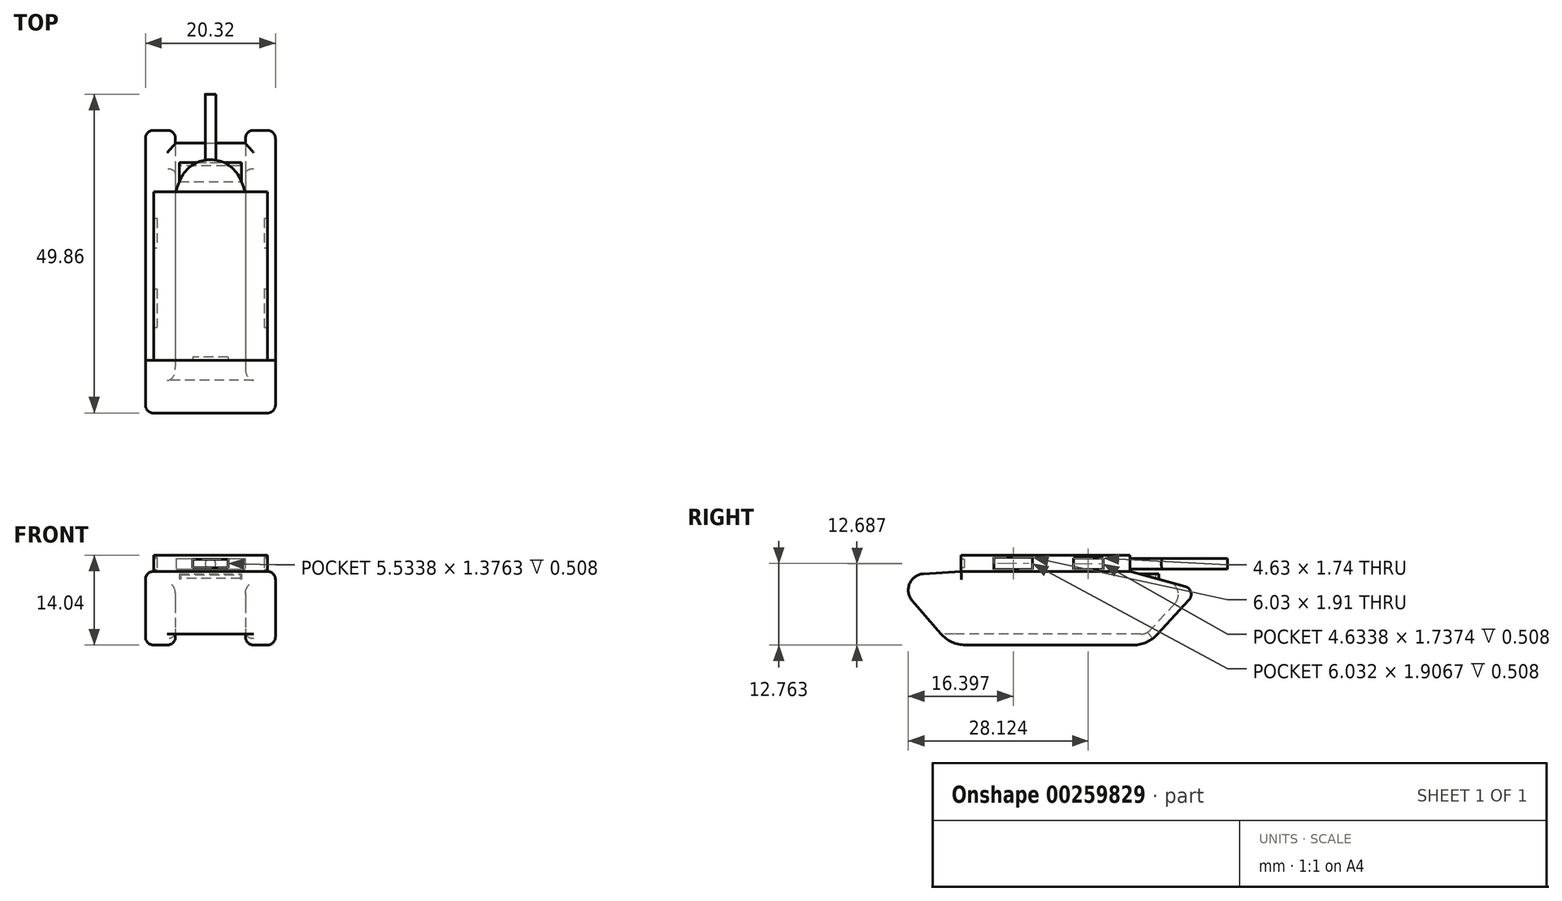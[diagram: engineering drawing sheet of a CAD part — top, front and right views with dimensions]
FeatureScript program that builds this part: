
annotation { "Feature Type Name" : "Feature", "Feature Type Description" : "" }
export const myFeature = defineFeature(function(context is Context, id is Id, definition is map)
    precondition{}
    {
        {
            var Q0;
            Q0=qCreatedBy(makeId("Right.planeOp"),FACE);
            var sketch = newSketch(context, id + "F0", { "sketchPlane" : qUnion([Q0])});
            skLineSegment(sketch, "E0", {"start": v(-16.04, 0) * mm, "end": v(14.77, 0) * mm});
            skLineSegment(sketch, "E1", {"start": v(14.77, 0) * mm, "end": v(22.64, 8.58) * mm});
            skLineSegment(sketch, "E2", {"start": v(22.64, 8.58) * mm, "end": v(12.15, 11.5) * mm});
            skLineSegment(sketch, "E3", {"start": v(12.15, 11.5) * mm, "end": v(-5.54, 11.5) * mm});
            skLineSegment(sketch, "E4", {"start": v(-5.54, 11.5) * mm, "end": v(-14.39, 11.5) * mm});
            skLineSegment(sketch, "E5", {"start": v(-14.39, 11.5) * mm, "end": v(-24.16, 14.6) * mm});
            skLineSegment(sketch, "E6", {"start": v(-24.16, 14.6) * mm, "end": v(-25.36, 10.8) * mm});
            skLineSegment(sketch, "E7", {"start": v(-14.39, 11.5) * mm, "end": v(-25.36, 10.8) * mm});
            skLineSegment(sketch, "E8", {"start": v(-25.36, 10.8) * mm, "end": v(-16.04, 0) * mm});
            skLineSegment(sketch, "E9", {"start": v(3.3, 11.5) * mm, "end": v(-3.22, 15.64) * mm});
            skLineSegment(sketch, "E10", {"start": v(-3.22, 15.64) * mm, "end": v(-10.54, 15.64) * mm});
            skLineSegment(sketch, "E11", {"start": v(-10.54, 15.64) * mm, "end": v(-10.54, 11.5) * mm});
            skSolve(sketch);
        }
        {
            var Q0;
            Q0=makeQuery(id+"F0.imprint","IMPRINT",FACE,{"disambiguationData":[TD([[makeQuery(id+"F0.imprint","IMPRINT",EDGE,{"derivedFrom":sQuery(id+"F0.wireOp",EDGE,"E0")}),1.0]])]});
            extrude(context, id + "F1", {"entities" : qUnion([Q0]), "depth" : 10.16 * mm});
        }
        {
            var Q0;
            Q0=makeQuery(id+"F1.opExtrude","CAP_FACE",FACE,{"disambiguationData":[OSD([sQuery(id+"F0.wireOp",EDGE,"E0"),sQuery(id+"F0.wireOp",EDGE,"E1"),sQuery(id+"F0.wireOp",EDGE,"E2"),sQuery(id+"F0.wireOp",EDGE,"E3"),sQuery(id+"F0.wireOp",EDGE,"E4"),sQuery(id+"F0.wireOp",EDGE,"E5"),sQuery(id+"F0.wireOp",EDGE,"E6"),sQuery(id+"F0.wireOp",EDGE,"E8")])],"isStart":true});
            extrude(context, id + "F2", {"entities" : qUnion([Q0]), "operationType" : NewBodyOperationType.ADD, "depth" : 10.16 * mm});
        }
        {
            var Q0;
            Q0=qCreatedBy(makeId("Front.planeOp"),FACE);
            var sketch = newSketch(context, id + "F3", { "sketchPlane" : qUnion([Q0])});
            skLineSegment(sketch, "E12.bottom", {"start": v(-5.47, 1.7) * mm, "end": v(5.47, 1.7) * mm});
            skLineSegment(sketch, "E12.top", {"start": v(-5.47, -1.7) * mm, "end": v(5.47, -1.7) * mm});
            skLineSegment(sketch, "E12.left", {"start": v(-5.47, 1.7) * mm, "end": v(-5.47, -1.7) * mm});
            skLineSegment(sketch, "E12.right", {"start": v(5.47, 1.7) * mm, "end": v(5.47, -1.7) * mm});
            skPoint(sketch, "E12.middle", {"position": v(0, 0) * mm});
            skSolve(sketch);
        }
        {
            var Q0;
            Q0=makeQuery(id+"F3.imprint","IMPRINT",FACE,{"disambiguationData":[TD([[makeQuery(id+"F3.imprint","IMPRINT",EDGE,{"derivedFrom":sQuery(id+"F3.wireOp",EDGE,"E12.bottom")}),-1.0]])]});
            extrude(context, id + "F4", {"entities" : qUnion([Q0]), "operationType" : NewBodyOperationType.REMOVE, "oppositeDirection" : true, "depth" : 25.4 * mm});
        }
        {
            var Q0;
            Q0=makeQuery(id+"F4.boolean.opBoolean","COPY",FACE,{"derivedFrom":makeQuery(id+"F4.opExtrude","CAP_FACE",FACE,{"disambiguationData":[OSD([sQuery(id+"F3.wireOp",EDGE,"E12.bottom"),sQuery(id+"F3.wireOp",EDGE,"E12.top"),sQuery(id+"F3.wireOp",EDGE,"E12.left"),sQuery(id+"F3.wireOp",EDGE,"E12.right")])],"isStart":true})});
            extrude(context, id + "F5", {"entities" : qUnion([Q0]), "operationType" : NewBodyOperationType.REMOVE, "oppositeDirection" : true, "depth" : 25.4 * mm});
        }
        {
            var Q0;
            {var subQ0=sQuery(id+"F0.wireOp",EDGE,"E0");var subQ1=sQuery(id+"F0.wireOp",EDGE,"E1");Q0=makeQuery(id+"F4.boolean.opBoolean","SPLIT",EDGE,{"disambiguationData":[TD([makeQuery(id+"F4.opExtrude","SWEPT_FACE",FACE,{"disambiguationData":[OSD([sQuery(id+"F3.wireOp",EDGE,"E12.right")])]})])],"derivedFrom":makeQuery(id+"F2.boolean.opBoolean","MERGE",EDGE,{"derivedFrom":[makeQuery(id+"F1.opExtrude","SWEPT_EDGE",EDGE,{"disambiguationData":[OSD([subQ0,subQ1])]}),makeQuery(id+"F2.opExtrude","SWEPT_EDGE",EDGE,{"disambiguationData":[OSD([subQ0,subQ1])]})]})});}
            var Q1;
            {var subQ0=sQuery(id+"F0.wireOp",EDGE,"E0");var subQ1=sQuery(id+"F0.wireOp",EDGE,"E8");var subQ2=sQuery(id+"F3.wireOp",EDGE,"E12.right");Q1=makeQuery(id+"F5.boolean.opBoolean","SPLIT",EDGE,{"disambiguationData":[TD([makeQuery(id+"F4.boolean.opBoolean","COPY",FACE,{"derivedFrom":makeQuery(id+"F4.opExtrude","SWEPT_FACE",FACE,{"disambiguationData":[OSD([subQ2])]})})])],"derivedFrom":makeQuery(id+"F2.boolean.opBoolean","MERGE",EDGE,{"derivedFrom":[makeQuery(id+"F1.opExtrude","SWEPT_EDGE",EDGE,{"disambiguationData":[OSD([subQ0,subQ1])]}),makeQuery(id+"F2.opExtrude","SWEPT_EDGE",EDGE,{"disambiguationData":[OSD([subQ0,subQ1])]})]})});}
            var Q2;
            {var subQ0=sQuery(id+"F0.wireOp",EDGE,"E1");var subQ1=sQuery(id+"F0.wireOp",EDGE,"E0");Q2=makeQuery(id+"F4.boolean.opBoolean","SPLIT",EDGE,{"disambiguationData":[TD([makeQuery(id+"F4.opExtrude","SWEPT_FACE",FACE,{"disambiguationData":[OSD([sQuery(id+"F3.wireOp",EDGE,"E12.left")])]})])],"derivedFrom":makeQuery(id+"F2.boolean.opBoolean","MERGE",EDGE,{"derivedFrom":[makeQuery(id+"F1.opExtrude","SWEPT_EDGE",EDGE,{"disambiguationData":[OSD([subQ1,subQ0])]}),makeQuery(id+"F2.opExtrude","SWEPT_EDGE",EDGE,{"disambiguationData":[OSD([subQ1,subQ0])]})]})});}
            fillet(context, id + "F6", {"entities" : qUnion([Q0, Q1, Q2]), "radius" : 5.08 * mm, "tangentPropagation" : true, "allowEdgeOverflow" : false});
        }
        {
            var Q0;
            {var subQ0=sQuery(id+"F0.wireOp",EDGE,"E2");var subQ1=sQuery(id+"F0.wireOp",EDGE,"E1");Q0=makeQuery(id+"F2.boolean.opBoolean","MERGE",EDGE,{"derivedFrom":[makeQuery(id+"F1.opExtrude","SWEPT_EDGE",EDGE,{"disambiguationData":[OSD([subQ1,subQ0])]}),makeQuery(id+"F2.opExtrude","SWEPT_EDGE",EDGE,{"disambiguationData":[OSD([subQ1,subQ0])]})]});}
            var Q1;
            {var subQ0=sQuery(id+"F0.wireOp",EDGE,"E3");var subQ1=sQuery(id+"F0.wireOp",EDGE,"E2");Q1=makeQuery(id+"F2.boolean.opBoolean","MERGE",EDGE,{"derivedFrom":[makeQuery(id+"F1.opExtrude","SWEPT_EDGE",EDGE,{"disambiguationData":[OSD([subQ1,subQ0])]}),makeQuery(id+"F2.opExtrude","SWEPT_EDGE",EDGE,{"disambiguationData":[OSD([subQ1,subQ0])]})]});}
            fillet(context, id + "F7", {"entities" : qUnion([Q0, Q1]), "radius" : 1.27 * mm, "tangentPropagation" : true, "allowEdgeOverflow" : false});
        }
        {
            var Q0;
            Q0=makeQuery(id+"F2.opExtrude","CAP_EDGE",EDGE,{"disambiguationData":[OSD([sQuery(id+"F0.wireOp",EDGE,"E3"),sQuery(id+"F0.wireOp",EDGE,"E4")])],"isStart":false});
            var Q1;
            Q1=makeQuery(id+"F1.opExtrude","CAP_EDGE",EDGE,{"disambiguationData":[OSD([sQuery(id+"F0.wireOp",EDGE,"E3"),sQuery(id+"F0.wireOp",EDGE,"E4")])],"isStart":false});
            fillet(context, id + "F8", {"entities" : qUnion([Q0, Q1]), "radius" : 1.27 * mm, "tangentPropagation" : true, "allowEdgeOverflow" : false});
        }
        {
            var Q0;
            {var subQ0=sQuery(id+"F0.wireOp",EDGE,"E1");Q0=makeQuery(id+"F2.boolean.opBoolean","MERGE",FACE,{"derivedFrom":[makeQuery(id+"F1.opExtrude","SWEPT_FACE",FACE,{"disambiguationData":[OSD([subQ0])]}),makeQuery(id+"F2.opExtrude","SWEPT_FACE",FACE,{"disambiguationData":[OSD([subQ0])]})]});}
            var sketch = newSketch(context, id + "F9", { "sketchPlane" : qUnion([Q0])});
            skLineSegment(sketch, "E13.bottom", {"start": v(5.47, 22) * mm, "end": v(-5.47, 22) * mm});
            skLineSegment(sketch, "E13.top", {"start": v(5.47, 2.57) * mm, "end": v(-5.47, 2.57) * mm});
            skLineSegment(sketch, "E13.left", {"start": v(5.47, 22) * mm, "end": v(5.47, 2.57) * mm});
            skLineSegment(sketch, "E13.right", {"start": v(-5.47, 22) * mm, "end": v(-5.47, 2.57) * mm});
            skPoint(sketch, "E13.middle", {"position": v(0, 12.29) * mm});
            skSolve(sketch);
        }
        {
            var Q0;
            {var subQ1=sQuery(id+"F0.wireOp",EDGE,"E1");var subQ2=makeQuery(id+"F2.boolean.opBoolean","MERGE",FACE,{"derivedFrom":[makeQuery(id+"F1.opExtrude","SWEPT_FACE",FACE,{"disambiguationData":[OSD([subQ1])]}),makeQuery(id+"F2.opExtrude","SWEPT_FACE",FACE,{"disambiguationData":[OSD([subQ1])]})]});var subQ3=makeQuery(id+"F4.boolean.opBoolean","INTERSECT",EDGE,{"derivedFrom":[subQ2,makeQuery(id+"F4.opExtrude","SWEPT_FACE",FACE,{"disambiguationData":[OSD([sQuery(id+"F3.wireOp",EDGE,"E12.bottom")])]})]});Q0=makeQuery(id+"F9.imprint","IMPRINT",FACE,{"disambiguationData":[TD([[makeQuery(id+"F9.imprint","IMPRINT",EDGE,{"derivedFrom":subQ3}),-1.0]])]});}
            var Q1;
            {var subQ0=sQuery(id+"F9.wireOp",EDGE,"E13.bottom");Q1=makeQuery(id+"F9.imprint","IMPRINT",FACE,{"disambiguationData":[TD([[makeQuery(id+"F9.imprint","IMPRINT",EDGE,{"derivedFrom":subQ0}),1.0]])]});}
            extrude(context, id + "F10", {"entities" : qUnion([Q0, Q1]), "operationType" : NewBodyOperationType.REMOVE, "oppositeDirection" : true, "depth" : 1.27 * mm});
        }
        {
            var Q0;
            Q0=makeQuery(id+"F10.boolean.opBoolean","COPY",FACE,{"derivedFrom":makeQuery(id+"F10.opExtrude","SWEPT_FACE",FACE,{"disambiguationData":[OSD([sQuery(id+"F0.wireOp",EDGE,"E1"),sQuery(id+"F3.wireOp",EDGE,"E12.bottom")])]})});
            extrude(context, id + "F11", {"entities" : qUnion([Q0]), "operationType" : NewBodyOperationType.REMOVE, "oppositeDirection" : true, "depth" : 1.27 * mm});
        }
        {
            var Q0;
            {var subQ0=sQuery(id+"F0.wireOp",EDGE,"E8");Q0=makeQuery(id+"F2.boolean.opBoolean","MERGE",FACE,{"derivedFrom":[makeQuery(id+"F1.opExtrude","SWEPT_FACE",FACE,{"disambiguationData":[OSD([subQ0])]}),makeQuery(id+"F2.opExtrude","SWEPT_FACE",FACE,{"disambiguationData":[OSD([subQ0])]})]});}
            var sketch = newSketch(context, id + "F12", { "sketchPlane" : qUnion([Q0])});
            skLineSegment(sketch, "E14.bottom", {"start": v(5.47, 31.97) * mm, "end": v(-5.47, 31.97) * mm});
            skLineSegment(sketch, "E14.top", {"start": v(5.47, -6.36) * mm, "end": v(-5.47, -6.36) * mm});
            skLineSegment(sketch, "E14.left", {"start": v(5.47, 31.97) * mm, "end": v(5.47, -6.36) * mm});
            skLineSegment(sketch, "E14.right", {"start": v(-5.47, 31.97) * mm, "end": v(-5.47, -6.36) * mm});
            skPoint(sketch, "E14.middle", {"position": v(0, 12.8) * mm});
            skSolve(sketch);
        }
        {
            var Q0;
            {var subQ0=sQuery(id+"F12.wireOp",EDGE,"E14.left");var subQ1=sQuery(id+"F0.wireOp",EDGE,"E8");var subQ2=makeQuery(id+"F2.opExtrude","SWEPT_FACE",FACE,{"disambiguationData":[OSD([subQ1])]});var subQ3=makeQuery(id+"F1.opExtrude","SWEPT_FACE",FACE,{"disambiguationData":[OSD([subQ1])]});var subQ4=makeQuery(id+"F2.boolean.opBoolean","MERGE",FACE,{"derivedFrom":[subQ3,subQ2]});var subQ5=sQuery(id+"F0.wireOp",EDGE,"E7");var subQ6=sQuery(id+"F0.wireOp",EDGE,"E6");var subQ7=makeQuery(id+"FmgriYv2DjoOcs5_1.opFillet","BLEND_EDGE",EDGE,{"blendedFrom":[makeQuery(id+"F2.boolean.opBoolean","MERGE",EDGE,{"derivedFrom":[makeQuery(id+"F1.opExtrude","SWEPT_EDGE",EDGE,{"disambiguationData":[OSD([subQ6,subQ5,subQ1])]}),makeQuery(id+"F2.opExtrude","SWEPT_EDGE",EDGE,{"disambiguationData":[OSD([subQ6,subQ5,subQ1])]})]}),subQ4],"blendedInto":[subQ4]});var subQ8=makeQuery(id+"F12.imprint","INTERSECT",VERTEX,{"derivedFrom":[subQ7,subQ0]});Q0=makeQuery(id+"F12.imprint","IMPRINT",FACE,{"disambiguationData":[TD([[makeQuery(id+"F12.imprint","IMPRINT",EDGE,{"disambiguationData":[TD([[subQ8,-1.0]])],"derivedFrom":subQ7}),1.0]])]});}
            var Q1;
            {var subQ0=sQuery(id+"F12.wireOp",EDGE,"E14.bottom");Q1=makeQuery(id+"F12.imprint","IMPRINT",FACE,{"disambiguationData":[TD([[makeQuery(id+"F12.imprint","IMPRINT",EDGE,{"derivedFrom":subQ0}),1.0]])]});}
            extrude(context, id + "F13", {"entities" : qUnion([Q0, Q1]), "operationType" : NewBodyOperationType.REMOVE, "oppositeDirection" : true, "depth" : 1.27 * mm});
        }
        {
            var Q0;
            {var subQ0=sQuery(id+"F0.wireOp",EDGE,"E1");Q0=makeQuery(id+"F10.boolean.opBoolean","INTERSECT",EDGE,{"derivedFrom":[makeQuery(id+"F7.opFillet","BLEND_FACE",FACE,{"disambiguationData":[OSD([subQ0,sQuery(id+"F0.wireOp",EDGE,"E2")])]}),makeQuery(id+"F10.opExtrude","CAP_FACE",FACE,{"disambiguationData":[OSD([subQ0,sQuery(id+"F3.wireOp",EDGE,"E12.bottom"),sQuery(id+"F9.wireOp",EDGE,"E13.bottom"),sQuery(id+"F9.wireOp",EDGE,"E13.left"),sQuery(id+"F9.wireOp",EDGE,"E13.right")])],"isStart":false})]});}
            var Q1;
            {var subQ0=sQuery(id+"F0.wireOp",EDGE,"E6");Q1=makeQuery(id+"F13.boolean.opBoolean","INTERSECT",EDGE,{"derivedFrom":[makeQuery(id+"F2.boolean.opBoolean","MERGE",FACE,{"derivedFrom":[makeQuery(id+"F1.opExtrude","SWEPT_FACE",FACE,{"disambiguationData":[OSD([subQ0])]}),makeQuery(id+"F2.opExtrude","SWEPT_FACE",FACE,{"disambiguationData":[OSD([subQ0])]})]}),makeQuery(id+"F13.opExtrude","CAP_FACE",FACE,{"disambiguationData":[OSD([sQuery(id+"F0.wireOp",EDGE,"E0"),sQuery(id+"F0.wireOp",EDGE,"E8"),sQuery(id+"F12.wireOp",EDGE,"E14.bottom"),sQuery(id+"F12.wireOp",EDGE,"E14.left"),sQuery(id+"F12.wireOp",EDGE,"E14.right")])],"isStart":false})]});}
            var Q2;
            {var subQ0=sQuery(id+"F0.wireOp",EDGE,"E8");var subQ1=sQuery(id+"F0.wireOp",EDGE,"E0");var subQ2=sQuery(id+"F3.wireOp",EDGE,"E12.bottom");Q2=makeQuery(id+"Fq2m1Uq80MRG6K2_1.boolean.opBoolean","INTERSECT",EDGE,{"derivedFrom":[makeQuery(id+"F5.boolean.opBoolean","MERGE",FACE,{"derivedFrom":[makeQuery(id+"F4.boolean.opBoolean","COPY",FACE,{"derivedFrom":makeQuery(id+"F4.opExtrude","SWEPT_FACE",FACE,{"disambiguationData":[OSD([subQ2])]})}),makeQuery(id+"F5.opExtrude","SWEPT_FACE",FACE,{"disambiguationData":[OSD([subQ2])]})]}),makeQuery(id+"Fq2m1Uq80MRG6K2_1.opExtrude","SWEPT_FACE",FACE,{"disambiguationData":[OSD([subQ1,subQ0]),TDD([makeQuery(id+"F13.boolean.opBoolean","COPY",EDGE,{"derivedFrom":makeQuery(id+"F13.opExtrude","CAP_EDGE",EDGE,{"disambiguationData":[OSD([subQ1,subQ0])],"isStart":false})})])]})]});}
            var Q3;
            {var subQ0=sQuery(id+"F3.wireOp",EDGE,"E12.bottom");var subQ1=sQuery(id+"F0.wireOp",EDGE,"E1");Q3=makeQuery(id+"F11.boolean.opBoolean","INTERSECT",EDGE,{"derivedFrom":[makeQuery(id+"F5.boolean.opBoolean","MERGE",FACE,{"derivedFrom":[makeQuery(id+"F4.boolean.opBoolean","COPY",FACE,{"derivedFrom":makeQuery(id+"F4.opExtrude","SWEPT_FACE",FACE,{"disambiguationData":[OSD([subQ0])]})}),makeQuery(id+"F5.opExtrude","SWEPT_FACE",FACE,{"disambiguationData":[OSD([subQ0])]})]}),makeQuery(id+"F11.opExtrude","SWEPT_FACE",FACE,{"disambiguationData":[OSD([subQ1,subQ0]),TDD([makeQuery(id+"F10.boolean.opBoolean","COPY",EDGE,{"derivedFrom":makeQuery(id+"F10.opExtrude","CAP_EDGE",EDGE,{"disambiguationData":[OSD([subQ1,subQ0])],"isStart":false})})])]})]});}
            fillet(context, id + "F14", {"entities" : qUnion([Q0, Q1, Q2, Q3]), "radius" : 2.03 * mm, "tangentPropagation" : true, "allowEdgeOverflow" : false});
        }
        {
            var Q0;
            {var subQ0=sQuery(id+"F0.wireOp",EDGE,"E1");Q0=makeQuery(id+"F11.boolean.opBoolean","MERGE",EDGE,{"derivedFrom":[makeQuery(id+"F4.boolean.opBoolean","INTERSECT",EDGE,{"derivedFrom":[makeQuery(id+"F2.boolean.opBoolean","MERGE",FACE,{"derivedFrom":[makeQuery(id+"F1.opExtrude","SWEPT_FACE",FACE,{"disambiguationData":[OSD([subQ0])]}),makeQuery(id+"F2.opExtrude","SWEPT_FACE",FACE,{"disambiguationData":[OSD([subQ0])]})]}),makeQuery(id+"F4.opExtrude","SWEPT_FACE",FACE,{"disambiguationData":[OSD([sQuery(id+"F3.wireOp",EDGE,"E12.left")])]})]}),makeQuery(id+"F10.boolean.opBoolean","COPY",EDGE,{"derivedFrom":makeQuery(id+"F10.opExtrude","CAP_EDGE",EDGE,{"disambiguationData":[OSD([sQuery(id+"F9.wireOp",EDGE,"E13.left")])],"isStart":true})})]});}
            var Q1;
            {var subQ0=sQuery(id+"F0.wireOp",EDGE,"E1");Q1=makeQuery(id+"F11.boolean.opBoolean","MERGE",EDGE,{"derivedFrom":[makeQuery(id+"F4.boolean.opBoolean","INTERSECT",EDGE,{"derivedFrom":[makeQuery(id+"F2.boolean.opBoolean","MERGE",FACE,{"derivedFrom":[makeQuery(id+"F1.opExtrude","SWEPT_FACE",FACE,{"disambiguationData":[OSD([subQ0])]}),makeQuery(id+"F2.opExtrude","SWEPT_FACE",FACE,{"disambiguationData":[OSD([subQ0])]})]}),makeQuery(id+"F4.opExtrude","SWEPT_FACE",FACE,{"disambiguationData":[OSD([sQuery(id+"F3.wireOp",EDGE,"E12.right")])]})]}),makeQuery(id+"F10.boolean.opBoolean","COPY",EDGE,{"derivedFrom":makeQuery(id+"F10.opExtrude","CAP_EDGE",EDGE,{"disambiguationData":[OSD([sQuery(id+"F9.wireOp",EDGE,"E13.right")])],"isStart":true})})]});}
            fillet(context, id + "F15", {"entities" : qUnion([Q0, Q1]), "radius" : 1.27 * mm, "tangentPropagation" : true, "allowEdgeOverflow" : false});
        }
        {
            var Q0;
            {var subQ0=sQuery(id+"F0.wireOp",EDGE,"E8");var subQ1=sQuery(id+"F0.wireOp",EDGE,"E7");var subQ2=sQuery(id+"F0.wireOp",EDGE,"E6");Q0=makeQuery(id+"F2.boolean.opBoolean","MERGE",EDGE,{"derivedFrom":[makeQuery(id+"F1.opExtrude","SWEPT_EDGE",EDGE,{"disambiguationData":[OSD([subQ2,subQ1,subQ0])]}),makeQuery(id+"F2.opExtrude","SWEPT_EDGE",EDGE,{"disambiguationData":[OSD([subQ2,subQ1,subQ0])]})]});}
            fillet(context, id + "F16", {"entities" : qUnion([Q0]), "radius" : 2.54 * mm, "tangentPropagation" : true, "allowEdgeOverflow" : false});
        }
        {
            var Q0;
            Q0=qCreatedBy(makeId("Front.planeOp"),FACE);
            var sketch = newSketch(context, id + "F17", { "sketchPlane" : qUnion([Q0])});
            skLineSegment(sketch, "E15.bottom", {"start": v(-4.86, 11.12) * mm, "end": v(4.86, 11.12) * mm});
            skLineSegment(sketch, "E15.top", {"start": v(-4.86, 10.04) * mm, "end": v(4.86, 10.04) * mm});
            skLineSegment(sketch, "E15.left", {"start": v(-4.86, 11.12) * mm, "end": v(-4.86, 10.04) * mm});
            skLineSegment(sketch, "E15.right", {"start": v(4.86, 11.12) * mm, "end": v(4.86, 10.04) * mm});
            skPoint(sketch, "E15.middle", {"position": v(0, 10.58) * mm});
            skLineSegment(sketch, "E16.bottom", {"start": v(-4.7, 10.97) * mm, "end": v(4.7, 10.97) * mm});
            skLineSegment(sketch, "E16.top", {"start": v(-4.7, 10.18) * mm, "end": v(4.7, 10.18) * mm});
            skLineSegment(sketch, "E16.left", {"start": v(-4.7, 10.97) * mm, "end": v(-4.7, 10.18) * mm});
            skLineSegment(sketch, "E16.right", {"start": v(4.7, 10.97) * mm, "end": v(4.7, 10.18) * mm});
            skLineSegment(sketch, "E17.bottom", {"start": v(-4.86, 9.41) * mm, "end": v(4.86, 9.41) * mm});
            skLineSegment(sketch, "E17.top", {"start": v(-4.86, 7.44) * mm, "end": v(4.86, 7.44) * mm});
            skLineSegment(sketch, "E17.left", {"start": v(-4.86, 9.41) * mm, "end": v(-4.86, 7.44) * mm});
            skLineSegment(sketch, "E17.right", {"start": v(4.86, 9.41) * mm, "end": v(4.86, 7.44) * mm});
            skPoint(sketch, "E17.middle", {"position": v(0, 8.43) * mm});
            skSolve(sketch);
        }
        {
            var Q0;
            Q0=makeQuery(id+"F17.imprint","IMPRINT",FACE,{"disambiguationData":[TD([[makeQuery(id+"F17.imprint","IMPRINT",EDGE,{"derivedFrom":sQuery(id+"F17.wireOp",EDGE,"E15.bottom")}),-1.0]])]});
            extrude(context, id + "F18", {"entities" : qUnion([Q0]), "oppositeDirection" : true, "depth" : 16.5 * mm});
        }
        {
            var Q0;
            {var subQ0=sQuery(id+"F0.wireOp",EDGE,"E4");var subQ1=sQuery(id+"F0.wireOp",EDGE,"E3");Q0=makeQuery(id+"F2.boolean.opBoolean","MERGE",FACE,{"derivedFrom":[makeQuery(id+"F1.opExtrude","SWEPT_FACE",FACE,{"disambiguationData":[OSD([subQ1,subQ0])]}),makeQuery(id+"F2.opExtrude","SWEPT_FACE",FACE,{"disambiguationData":[OSD([subQ1,subQ0])]})]});}
            extrude(context, id + "F19", {"entities" : qUnion([Q0]), "operationType" : NewBodyOperationType.ADD, "depth" : 2.54 * mm});
        }
        {
            var Q0;
            {var subQ0=sQuery(id+"F0.wireOp",EDGE,"E4");var subQ1=sQuery(id+"F0.wireOp",EDGE,"E3");Q0=makeQuery(id+"F19.opExtrude","SWEPT_FACE",FACE,{"disambiguationData":[OSD([subQ1,subQ0]),TDD([makeQuery(id+"F8.opFillet","BLEND_EDGE",EDGE,{"blendedFrom":[makeQuery(id+"F1.opExtrude","CAP_EDGE",EDGE,{"disambiguationData":[OSD([subQ1,subQ0])],"isStart":false}),makeQuery(id+"F2.boolean.opBoolean","MERGE",FACE,{"derivedFrom":[makeQuery(id+"F1.opExtrude","SWEPT_FACE",FACE,{"disambiguationData":[OSD([subQ1,subQ0])]}),makeQuery(id+"F2.opExtrude","SWEPT_FACE",FACE,{"disambiguationData":[OSD([subQ1,subQ0])]})]})],"blendedInto":[makeQuery(id+"F2.boolean.opBoolean","MERGE",FACE,{"derivedFrom":[makeQuery(id+"F1.opExtrude","SWEPT_FACE",FACE,{"disambiguationData":[OSD([subQ1,subQ0])]}),makeQuery(id+"F2.opExtrude","SWEPT_FACE",FACE,{"disambiguationData":[OSD([subQ1,subQ0])]})]})]})])]});}
            var sketch = newSketch(context, id + "F20", { "sketchPlane" : qUnion([Q0])});
            skLineSegment(sketch, "E18.bottom", {"start": v(7.8, 13.56) * mm, "end": v(3.17, 13.56) * mm});
            skLineSegment(sketch, "E18.top", {"start": v(7.8, 11.82) * mm, "end": v(3.17, 11.82) * mm});
            skLineSegment(sketch, "E18.left", {"start": v(7.8, 13.56) * mm, "end": v(7.8, 11.82) * mm});
            skLineSegment(sketch, "E18.right", {"start": v(3.17, 13.56) * mm, "end": v(3.17, 11.82) * mm});
            skPoint(sketch, "E18.middle", {"position": v(5.48, 12.69) * mm});
            skLineSegment(sketch, "E19.bottom", {"start": v(-3.23, 13.72) * mm, "end": v(-9.26, 13.72) * mm});
            skLineSegment(sketch, "E19.top", {"start": v(-3.23, 11.81) * mm, "end": v(-9.26, 11.81) * mm});
            skLineSegment(sketch, "E19.left", {"start": v(-3.23, 13.72) * mm, "end": v(-3.23, 11.81) * mm});
            skLineSegment(sketch, "E19.right", {"start": v(-9.26, 13.72) * mm, "end": v(-9.26, 11.81) * mm});
            skPoint(sketch, "E19.middle", {"position": v(-6.24, 12.76) * mm});
            skSolve(sketch);
        }
        {
            var Q0;
            Q0=makeQuery(id+"F20.imprint","IMPRINT",FACE,{"disambiguationData":[TD([[makeQuery(id+"F20.imprint","IMPRINT",EDGE,{"derivedFrom":sQuery(id+"F20.wireOp",EDGE,"E19.bottom")}),1.0]])]});
            var Q1;
            Q1=makeQuery(id+"F20.imprint","IMPRINT",FACE,{"disambiguationData":[TD([[makeQuery(id+"F20.imprint","IMPRINT",EDGE,{"derivedFrom":sQuery(id+"F20.wireOp",EDGE,"E18.bottom")}),1.0]])]});
            extrude(context, id + "F21", {"entities" : qUnion([Q0, Q1]), "operationType" : NewBodyOperationType.REMOVE, "oppositeDirection" : true, "depth" : 25.4 * mm});
        }
        {
            var Q0;
            Q0=makeQuery(id+"F20.imprint","IMPRINT",FACE,{"disambiguationData":[TD([[makeQuery(id+"F20.imprint","IMPRINT",EDGE,{"derivedFrom":sQuery(id+"F20.wireOp",EDGE,"E18.bottom")}),1.0]])]});
            var Q1;
            Q1=makeQuery(id+"F20.imprint","IMPRINT",FACE,{"disambiguationData":[TD([[makeQuery(id+"F20.imprint","IMPRINT",EDGE,{"derivedFrom":sQuery(id+"F20.wireOp",EDGE,"E19.bottom")}),1.0]])]});
            extrude(context, id + "F22", {"entities" : qUnion([Q0, Q1]), "operationType" : NewBodyOperationType.ADD, "oppositeDirection" : true, "depth" : 17.27 * mm});
        }
        {
            var Q0;
            Q0=makeQuery(id+"F20.imprint","IMPRINT",FACE,{"disambiguationData":[TD([[makeQuery(id+"F20.imprint","IMPRINT",EDGE,{"derivedFrom":sQuery(id+"F20.wireOp",EDGE,"E19.bottom")}),1.0]])]});
            var Q1;
            Q1=makeQuery(id+"F20.imprint","IMPRINT",FACE,{"disambiguationData":[TD([[makeQuery(id+"F20.imprint","IMPRINT",EDGE,{"derivedFrom":sQuery(id+"F20.wireOp",EDGE,"E18.bottom")}),1.0]])]});
            extrude(context, id + "F23", {"entities" : qUnion([Q0, Q1]), "operationType" : NewBodyOperationType.REMOVE, "oppositeDirection" : true, "depth" : 0.5 * mm});
        }
        {
            var Q0;
            Q0=makeQuery(id+"F17.imprint","IMPRINT",FACE,{"disambiguationData":[TD([[makeQuery(id+"F17.imprint","IMPRINT",EDGE,{"derivedFrom":sQuery(id+"F17.wireOp",EDGE,"E16.bottom")}),-1.0]])]});
            extrude(context, id + "F24", {"entities" : qUnion([Q0]), "operationType" : NewBodyOperationType.ADD, "oppositeDirection" : true, "depth" : 16 * mm});
        }
        {
            var Q0;
            Q0=makeQuery(id+"F19.opExtrude","SWEPT_FACE",FACE,{"disambiguationData":[OSD([sQuery(id+"F0.wireOp",EDGE,"E2"),sQuery(id+"F0.wireOp",EDGE,"E3"),sQuery(id+"F0.wireOp",EDGE,"E4")])]});
            var sketch = newSketch(context, id + "F25", { "sketchPlane" : qUnion([Q0])});
            skLineSegment(sketch, "E20.bottom", {"start": v(5.4, 13.5) * mm, "end": v(-5.4, 13.5) * mm});
            skLineSegment(sketch, "E20.top", {"start": v(5.4, 11.84) * mm, "end": v(-5.4, 11.84) * mm});
            skLineSegment(sketch, "E20.left", {"start": v(5.4, 13.5) * mm, "end": v(5.4, 11.84) * mm});
            skLineSegment(sketch, "E20.right", {"start": v(-5.4, 13.5) * mm, "end": v(-5.4, 11.84) * mm});
            skPoint(sketch, "E20.middle", {"position": v(0, 12.67) * mm});
            skCircle(sketch, "E21", {"center": v(0, 12.67) * mm, "radius": 0.82 * mm});
            skSolve(sketch);
        }
        {
            var Q0;
            {var subQ0=sQuery(id+"F25.wireOp",EDGE,"E20.right");Q0=makeQuery(id+"F25.imprint","IMPRINT",FACE,{"disambiguationData":[TD([[makeQuery(id+"F25.imprint","IMPRINT",EDGE,{"derivedFrom":subQ0}),1.0]])]});}
            var Q1;
            {var subQ0=sQuery(id+"F25.wireOp",EDGE,"E20.left");Q1=makeQuery(id+"F25.imprint","IMPRINT",FACE,{"disambiguationData":[TD([[makeQuery(id+"F25.imprint","IMPRINT",EDGE,{"derivedFrom":subQ0}),-1.0]])]});}
            var Q2;
            {var subQ0=sQuery(id+"F25.wireOp",EDGE,"E21");var subQ1=makeQuery(id+"F25.imprint","INTERSECT",VERTEX,{"derivedFrom":[sQuery(id+"F25.wireOp",EDGE,"E20.bottom"),subQ0]});Q2=makeQuery(id+"F25.imprint","IMPRINT",FACE,{"disambiguationData":[TD([[makeQuery(id+"F25.imprint","IMPRINT",EDGE,{"disambiguationData":[TD([[subQ1,-1.0]])],"derivedFrom":subQ0}),1.0]])]});}
            extrude(context, id + "F26", {"entities" : qUnion([Q0, Q1, Q2]), "operationType" : NewBodyOperationType.ADD, "depth" : 7.62 * mm});
        }
        {
            var Q0;
            Q0=makeQuery(id+"F26.opExtrude","CAP_EDGE",EDGE,{"disambiguationData":[OSD([sQuery(id+"F25.wireOp",EDGE,"E20.right")])],"isStart":false});
            var Q1;
            Q1=makeQuery(id+"F26.opExtrude","CAP_EDGE",EDGE,{"disambiguationData":[OSD([sQuery(id+"F25.wireOp",EDGE,"E20.left")])],"isStart":false});
            fillet(context, id + "F27", {"entities" : qUnion([Q0, Q1]), "radius" : 10.16 * mm, "tangentPropagation" : true, "allowEdgeOverflow" : false});
        }
        {
            var Q0;
            Q0=makeQuery(id+"F27.opFillet","BLEND_EDGE",EDGE,{"blendedFrom":[makeQuery(id+"F26.opExtrude","CAP_EDGE",EDGE,{"disambiguationData":[OSD([sQuery(id+"F25.wireOp",EDGE,"E20.left")])],"isStart":false}),makeQuery(id+"F26.opExtrude","CAP_EDGE",EDGE,{"disambiguationData":[OSD([sQuery(id+"F25.wireOp",EDGE,"E20.right")])],"isStart":false})],"blendedInto":[]});
            fillet(context, id + "F28", {"entities" : qUnion([Q0]), "radius" : 5.08 * mm, "tangentPropagation" : true, "allowEdgeOverflow" : false});
        }
        {
            var Q0;
            {var subQ0=sQuery(id+"F25.wireOp",EDGE,"E21");var subQ1=makeQuery(id+"F25.imprint","INTERSECT",VERTEX,{"derivedFrom":[sQuery(id+"F25.wireOp",EDGE,"E20.bottom"),subQ0]});Q0=makeQuery(id+"F25.imprint","IMPRINT",FACE,{"disambiguationData":[TD([[makeQuery(id+"F25.imprint","IMPRINT",EDGE,{"disambiguationData":[TD([[subQ1,-1.0]])],"derivedFrom":subQ0}),1.0]])]});}
            extrude(context, id + "F29", {"entities" : qUnion([Q0]), "operationType" : NewBodyOperationType.ADD, "depth" : 15.24 * mm});
        }
        {
            var Q0;
            Q0=makeQuery(id+"F19.opExtrude","SWEPT_FACE",FACE,{"disambiguationData":[OSD([sQuery(id+"F0.wireOp",EDGE,"E4"),sQuery(id+"F0.wireOp",EDGE,"E5"),sQuery(id+"F0.wireOp",EDGE,"E7")])]});
            var sketch = newSketch(context, id + "F30", { "sketchPlane" : qUnion([Q0])});
            skLineSegment(sketch, "E22.bottom", {"start": v(2.77, 13.42) * mm, "end": v(-2.77, 13.42) * mm});
            skLineSegment(sketch, "E22.top", {"start": v(2.77, 12.05) * mm, "end": v(-2.77, 12.05) * mm});
            skLineSegment(sketch, "E22.left", {"start": v(2.77, 13.42) * mm, "end": v(2.77, 12.05) * mm});
            skLineSegment(sketch, "E22.right", {"start": v(-2.77, 13.42) * mm, "end": v(-2.77, 12.05) * mm});
            skPoint(sketch, "E22.middle", {"position": v(0, 12.74) * mm});
            skSolve(sketch);
        }
        {
            var Q0;
            Q0=makeQuery(id+"F30.imprint","IMPRINT",FACE,{"disambiguationData":[TD([[makeQuery(id+"F30.imprint","IMPRINT",EDGE,{"derivedFrom":sQuery(id+"F30.wireOp",EDGE,"E22.bottom")}),1.0]])]});
            extrude(context, id + "F31", {"entities" : qUnion([Q0]), "operationType" : NewBodyOperationType.REMOVE, "oppositeDirection" : true, "depth" : 0.5 * mm});
        }
    });
